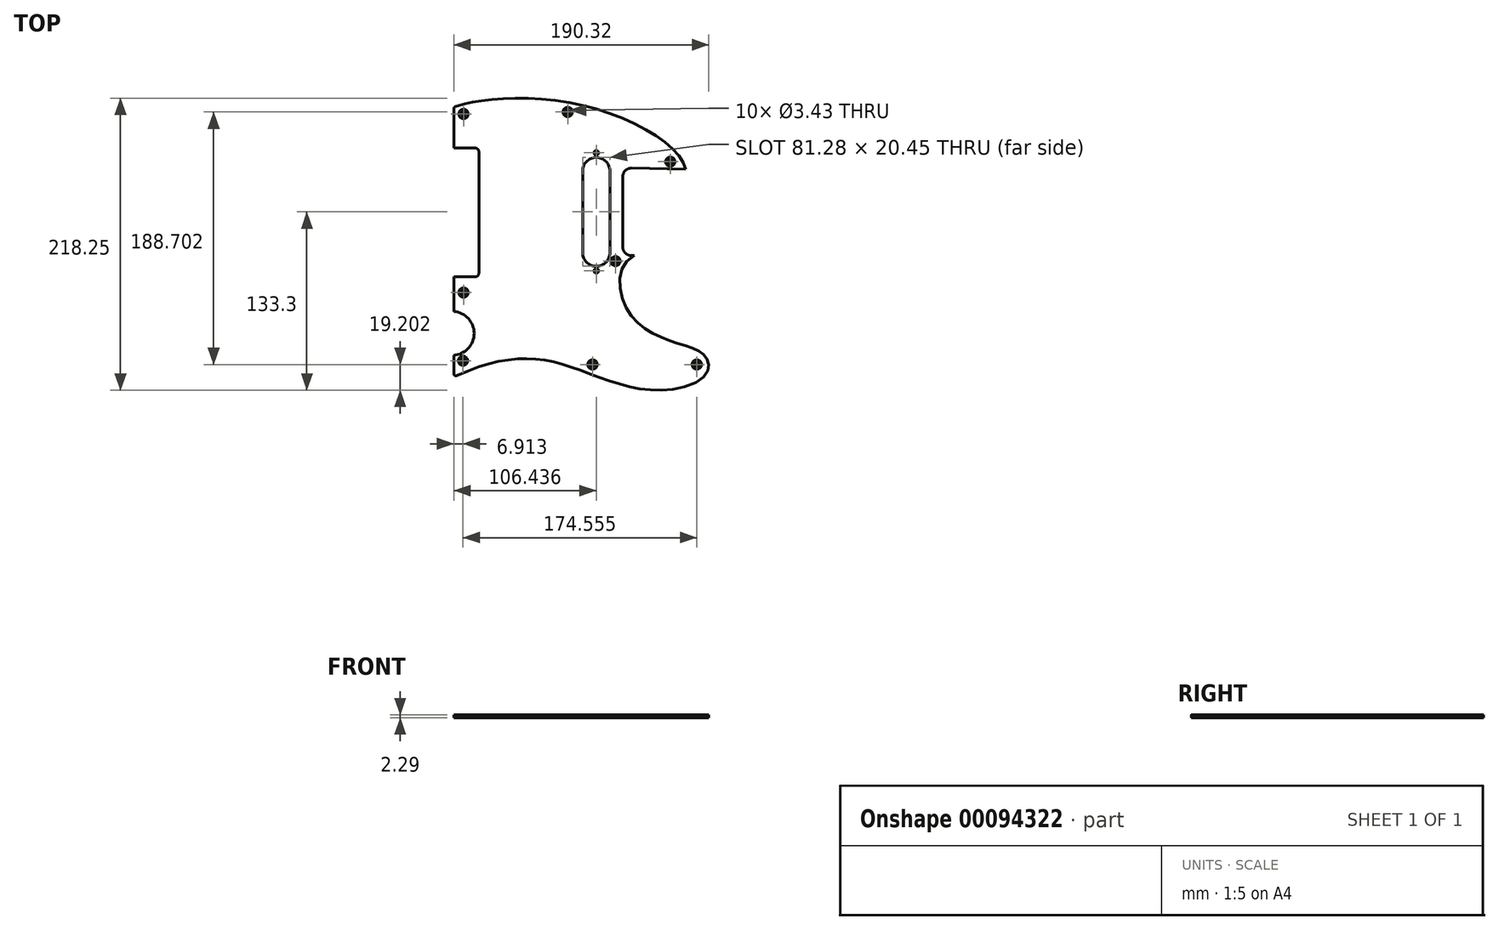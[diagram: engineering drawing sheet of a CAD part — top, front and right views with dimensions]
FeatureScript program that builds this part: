
annotation { "Feature Type Name" : "Feature", "Feature Type Description" : "" }
export const myFeature = defineFeature(function(context is Context, id is Id, definition is map)
    precondition{}
    {
        {
            var Q0;
            Q0=qCreatedBy(makeId("Top.planeOp"),FACE);
            var sketch = newSketch(context, id + "F0", { "sketchPlane" : qUnion([Q0])});
            skLineSegment(sketch, "E0", {"start": v(-107.32, 0) * mm, "end": v(-107.32, -45.47) * mm});
            skArc(sketch, "E1", {"start": v(-107.32, -45.47) * mm, "mid": v(-108.24, -47.71) * mm, "end": v(-110.5, -48.64) * mm});
            skLineSegment(sketch, "E2", {"start": v(-110.5, -48.64) * mm, "end": v(-126.18, -48.64) * mm});
            skLineSegment(sketch, "E3", {"start": v(-196.85, -112.5) * mm, "end": v(-196.85, 91.25) * mm, "construction": true});
            skLineSegment(sketch, "E4", {"start": v(0, 0) * mm, "end": v(0, -26.3) * mm});
            skLineSegment(sketch, "E5", {"start": v(0, 0) * mm, "end": v(0, 26.3) * mm});
            skLineSegment(sketch, "E6", {"start": v(0, 0) * mm, "end": v(-107.32, 0) * mm, "construction": true});
            skCircle(sketch, "E7", {"center": v(-19.74, 44.1) * mm, "radius": 1.71 * mm});
            skCircle(sketch, "E8.MirrorC", {"center": v(-19.74, -44.1) * mm, "radius": 1.71 * mm});
            skLineSegment(sketch, "E9", {"start": v(6.47, -32.64) * mm, "end": v(6.47, 0) * mm, "construction": true});
            skLineSegment(sketch, "E10", {"start": v(6.47, 0) * mm, "end": v(6.47, 32.64) * mm, "construction": true});
            skLineSegment(sketch, "E11", {"start": v(0, 0) * mm, "end": v(6.47, 0) * mm, "construction": true});
            skLineSegment(sketch, "E12", {"start": v(-29.97, 0) * mm, "end": v(-29.97, 30.42) * mm});
            skLineSegment(sketch, "E13", {"start": v(-19.74, 44.1) * mm, "end": v(-19.74, -44.1) * mm, "construction": true});
            skArc(sketch, "E14", {"start": v(-29.97, 30.42) * mm, "mid": v(-26.97, 37.65) * mm, "end": v(-19.74, 40.64) * mm});
            skArc(sketch, "E15.MirrorCS", {"start": v(-9.52, 30.42) * mm, "mid": v(-12.52, 37.65) * mm, "end": v(-19.74, 40.64) * mm});
            skLineSegment(sketch, "E16.MirrorCS", {"start": v(-9.52, 0) * mm, "end": v(-9.52, 30.42) * mm});
            skLineSegment(sketch, "E17", {"start": v(6.47, 32.64) * mm, "end": v(47, 31.88) * mm});
            skFitSpline(sketch, "E18", {"points": [v(47, 31.88) * mm, v(-44.08, 82.43) * mm, v(-126.18, 77.89) * mm], "startDerivative": vector(-27.84, 117.85) * mm, "endDerivative": vector(-42, -26.96) * mm});
            skArc(sketch, "E19", {"start": v(0, 26.3) * mm, "mid": v(1.9, 30.82) * mm, "end": v(6.47, 32.64) * mm});
            skArc(sketch, "E20.MirrorCS", {"start": v(0, -26.3) * mm, "mid": v(1.9, -30.82) * mm, "end": v(6.47, -32.64) * mm});
            skLineSegment(sketch, "E21", {"start": v(-107.32, 0) * mm, "end": v(-107.32, 44.58) * mm});
            skArc(sketch, "E22", {"start": v(-107.32, 44.58) * mm, "mid": v(-108.24, 46.82) * mm, "end": v(-110.5, 47.75) * mm});
            skLineSegment(sketch, "E23", {"start": v(-126.18, 47.75) * mm, "end": v(-126.18, 77) * mm});
            skLineSegment(sketch, "E24", {"start": v(-126.18, 47.75) * mm, "end": v(-110.5, 47.75) * mm});
            skLineSegment(sketch, "E25.MirrorCS", {"start": v(-29.97, 0) * mm, "end": v(-29.97, -30.42) * mm});
            skArc(sketch, "E26.MirrorCS", {"start": v(-29.97, -30.42) * mm, "mid": v(-26.97, -37.65) * mm, "end": v(-19.74, -40.64) * mm});
            skArc(sketch, "E27.MirrorCS", {"start": v(-9.52, -30.42) * mm, "mid": v(-12.52, -37.65) * mm, "end": v(-19.74, -40.64) * mm});
            skLineSegment(sketch, "E28.MirrorCS", {"start": v(-9.52, 0) * mm, "end": v(-9.52, -30.42) * mm});
            skLineSegment(sketch, "E29", {"start": v(-126.18, -48.64) * mm, "end": v(-126.18, -74.46) * mm});
            skArc(sketch, "E30", {"start": v(-126.18, -107.15) * mm, "mid": v(-110.94, -90.8) * mm, "end": v(-126.18, -74.46) * mm});
            skLineSegment(sketch, "E31", {"start": v(-126.18, -107.15) * mm, "end": v(-126.18, -121) * mm});
            skArc(sketch, "E32", {"start": v(-126.18, -121) * mm, "mid": v(-125.49, -122.28) * mm, "end": v(-124.04, -122.4) * mm});
            skFitSpline(sketch, "E33", {"points": [v(-124.04, -122.4) * mm, v(-44.44, -114.06) * mm, v(45.98, -130.85) * mm], "startDerivative": vector(198.13, 88.7) * mm, "endDerivative": vector(201.41, 51.9) * mm});
            skFitSpline(sketch, "E34", {"points": [v(45.98, -130.85) * mm, v(62.7, -109.4) * mm, v(40.06, -97.97) * mm, v(3.96, -74.04) * mm, v(8.48, -32.6) * mm], "startDerivative": vector(240.17, 61.88) * mm, "endDerivative": vector(155.7, 80.37) * mm});
            skLineSegment(sketch, "E35", {"start": v(6.47, -32.64) * mm, "end": v(8.48, -32.6) * mm});
            skPoint(sketch, "E36", {"position": v(-110.94, -90.8) * mm});
            skArc(sketch, "E37.filletArc", {"start": v(-125.34, 78.36) * mm, "mid": v(-125.95, 77.8) * mm, "end": v(-126.18, 77) * mm});
            skSolve(sketch);
        }
        {
            var Q0;
            Q0 = qSketchRegion(id + "F0", true);
            extrude(context, id + "F1", {"entities" : qUnion([Q0]), "depth" : 2.3 * mm});
        }
        {
            var Q0;
            Q0=makeQuery(id+"F1.opExtrude","CAP_FACE",FACE,{"disambiguationData":[OSD([sQuery(id+"F0.wireOp",EDGE,"E0"),sQuery(id+"F0.wireOp",EDGE,"E1"),sQuery(id+"F0.wireOp",EDGE,"E2"),sQuery(id+"F0.wireOp",EDGE,"E4"),sQuery(id+"F0.wireOp",EDGE,"E5"),sQuery(id+"F0.wireOp",EDGE,"E7"),sQuery(id+"F0.wireOp",EDGE,"E8.MirrorC"),sQuery(id+"F0.wireOp",EDGE,"E12"),sQuery(id+"F0.wireOp",EDGE,"E14"),sQuery(id+"F0.wireOp",EDGE,"E15.MirrorCS"),sQuery(id+"F0.wireOp",EDGE,"E16.MirrorCS"),sQuery(id+"F0.wireOp",EDGE,"E17"),sQuery(id+"F0.wireOp",EDGE,"E18"),sQuery(id+"F0.wireOp",EDGE,"E19"),sQuery(id+"F0.wireOp",EDGE,"E20.MirrorCS"),sQuery(id+"F0.wireOp",EDGE,"E21"),sQuery(id+"F0.wireOp",EDGE,"E22"),sQuery(id+"F0.wireOp",EDGE,"E23"),sQuery(id+"F0.wireOp",EDGE,"E24"),sQuery(id+"F0.wireOp",EDGE,"E25.MirrorCS"),sQuery(id+"F0.wireOp",EDGE,"E26.MirrorCS"),sQuery(id+"F0.wireOp",EDGE,"E27.MirrorCS"),sQuery(id+"F0.wireOp",EDGE,"E28.MirrorCS"),sQuery(id+"F0.wireOp",EDGE,"E29"),sQuery(id+"F0.wireOp",EDGE,"E30"),sQuery(id+"F0.wireOp",EDGE,"E31"),sQuery(id+"F0.wireOp",EDGE,"E32"),sQuery(id+"F0.wireOp",EDGE,"E33"),sQuery(id+"F0.wireOp",EDGE,"E34"),sQuery(id+"F0.wireOp",EDGE,"E35"),sQuery(id+"F0.wireOp",EDGE,"E37.filletArc")])],"isStart":false});
            var sketch = newSketch(context, id + "F2", { "sketchPlane" : qUnion([Q0])});
            skPoint(sketch, "E38", {"position": v(-118.9, 73.14) * mm});
            skPoint(sketch, "E39", {"position": v(-41.07, 74.6) * mm});
            skPoint(sketch, "E40", {"position": v(35.47, 37.44) * mm});
            skPoint(sketch, "E41", {"position": v(-5.42, -36.82) * mm});
            skPoint(sketch, "E42", {"position": v(55.29, -114.08) * mm});
            skPoint(sketch, "E43", {"position": v(-22.59, -114.1) * mm});
            skPoint(sketch, "E44", {"position": v(-119.27, -111.27) * mm});
            skPoint(sketch, "E45", {"position": v(-118.87, -60.33) * mm});
            skSolve(sketch);
        }
        {
            var Q0;
            Q0=sQuery(id+"F2.wireOp",VERTEX,"E38");
            var Q1;
            Q1=sQuery(id+"F2.wireOp",VERTEX,"E39");
            var Q2;
            Q2=sQuery(id+"F2.wireOp",VERTEX,"E40");
            var Q3;
            Q3=sQuery(id+"F2.wireOp",VERTEX,"E41");
            var Q4;
            Q4=sQuery(id+"F2.wireOp",VERTEX,"E43");
            var Q5;
            Q5=sQuery(id+"F2.wireOp",VERTEX,"E42");
            var Q6;
            Q6=sQuery(id+"F2.wireOp",VERTEX,"E44");
            var Q7;
            Q7=sQuery(id+"F2.wireOp",VERTEX,"E45");
            var Q8;
            Q8=makeQuery(id+"F1.opExtrude","SWEPT_BODY",BODY,{"disambiguationData":[OSD([sQuery(id+"F0.wireOp",EDGE,"E0"),sQuery(id+"F0.wireOp",EDGE,"E1"),sQuery(id+"F0.wireOp",EDGE,"E2"),sQuery(id+"F0.wireOp",EDGE,"E4"),sQuery(id+"F0.wireOp",EDGE,"E5"),sQuery(id+"F0.wireOp",EDGE,"E7"),sQuery(id+"F0.wireOp",EDGE,"E8.MirrorC"),sQuery(id+"F0.wireOp",EDGE,"E12"),sQuery(id+"F0.wireOp",EDGE,"E14"),sQuery(id+"F0.wireOp",EDGE,"E15.MirrorCS"),sQuery(id+"F0.wireOp",EDGE,"E16.MirrorCS"),sQuery(id+"F0.wireOp",EDGE,"E17"),sQuery(id+"F0.wireOp",EDGE,"E18"),sQuery(id+"F0.wireOp",EDGE,"E19"),sQuery(id+"F0.wireOp",EDGE,"E20.MirrorCS"),sQuery(id+"F0.wireOp",EDGE,"E21"),sQuery(id+"F0.wireOp",EDGE,"E22"),sQuery(id+"F0.wireOp",EDGE,"E23"),sQuery(id+"F0.wireOp",EDGE,"E24"),sQuery(id+"F0.wireOp",EDGE,"E25.MirrorCS"),sQuery(id+"F0.wireOp",EDGE,"E26.MirrorCS"),sQuery(id+"F0.wireOp",EDGE,"E27.MirrorCS"),sQuery(id+"F0.wireOp",EDGE,"E28.MirrorCS"),sQuery(id+"F0.wireOp",EDGE,"E29"),sQuery(id+"F0.wireOp",EDGE,"E30"),sQuery(id+"F0.wireOp",EDGE,"E31"),sQuery(id+"F0.wireOp",EDGE,"E32"),sQuery(id+"F0.wireOp",EDGE,"E33"),sQuery(id+"F0.wireOp",EDGE,"E34"),sQuery(id+"F0.wireOp",EDGE,"E35"),sQuery(id+"F0.wireOp",EDGE,"E37.filletArc")])]});
            hole(context, id + "F3", {"style" : HoleStyle.C_SINK, "endStyle" : HoleEndStyle.THROUGH, "holeDiameter" : 3.43 * mm, "cSinkDiameter" : 7 * mm, "cSinkAngle" : 100 * degree, "tappedDepth" : 12.7 * mm, "tapClearance" : 3, "startFromSketch" : true, "locations" : qUnion([Q0, Q1, Q2, Q3, Q4, Q5, Q6, Q7]), "scope" : qUnion([Q8])});
        }
    });
